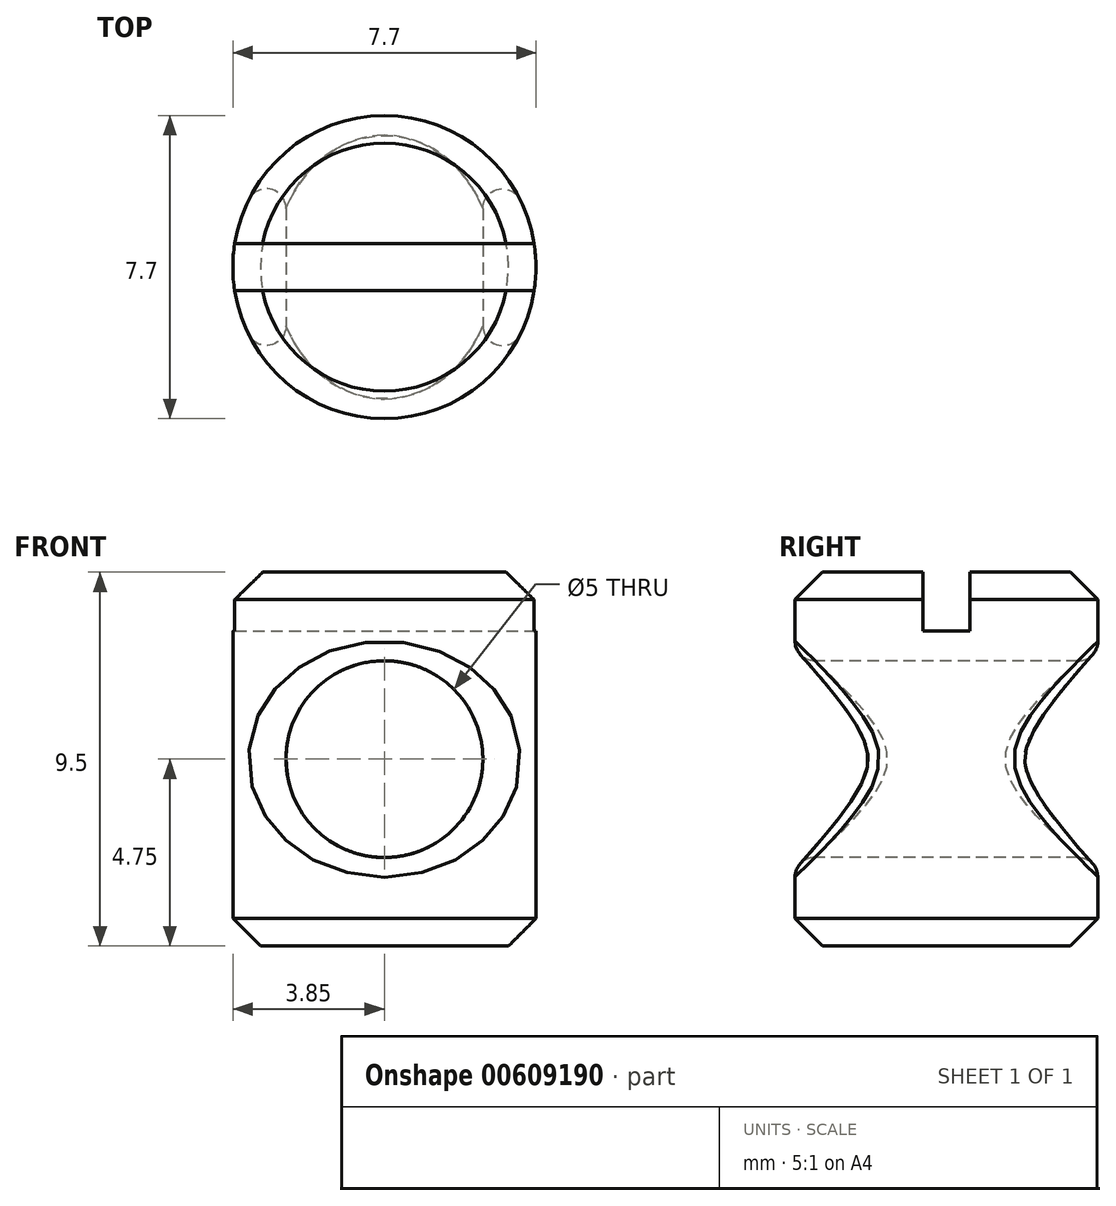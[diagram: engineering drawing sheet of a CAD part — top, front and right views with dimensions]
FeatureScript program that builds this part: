
annotation { "Feature Type Name" : "Feature", "Feature Type Description" : "" }
export const myFeature = defineFeature(function(context is Context, id is Id, definition is map)
    precondition{}
    {
        {
            var Q0;
            Q0=qCreatedBy(makeId("Top.planeOp"),FACE);
            var sketch = newSketch(context, id + "F0", { "sketchPlane" : qUnion([Q0])});
            skCircle(sketch, "E0", {"center": v(0, 0) * mm, "radius": 3.85 * mm});
            skSolve(sketch);
        }
        {
            var Q0;
            Q0=qSketchRegion(id+"F0",true);
            extrude(context, id + "F1", {"entities" : qUnion([Q0]), "depth" : 9.5 * mm, "offsetDistance" : 25 * mm});
        }
        {
            var Q0;
            Q0=qCreatedBy(makeId("Front.planeOp"),FACE);
            var sketch = newSketch(context, id + "F2", { "sketchPlane" : qUnion([Q0])});
            skCircle(sketch, "E1", {"center": v(0, 4.75) * mm, "radius": 2.5 * mm});
            skSolve(sketch);
        }
        {
            var Q0;
            Q0=qSketchRegion(id+"F2",true);
            extrude(context, id + "F3", {"entities" : qUnion([Q0]), "operationType" : NewBodyOperationType.REMOVE, "endBound" : BoundingType.SYMMETRIC, "oppositeDirection" : true, "depth" : 25 * mm, "offsetDistance" : 25 * mm});
        }
        {
            var Q0;
            Q0=makeQuery(id+"F1.opExtrude","CAP_FACE",FACE,{"disambiguationData":[OSD([sQuery(id+"F0.wireOp",EDGE,"E0")])],"isStart":false});
            var sketch = newSketch(context, id + "F4", { "sketchPlane" : qUnion([Q0])});
            skLineSegment(sketch, "E2.bottom", {"start": v(-4.71, 0.6) * mm, "end": v(4.71, 0.6) * mm});
            skLineSegment(sketch, "E2.top", {"start": v(-4.71, -0.6) * mm, "end": v(4.71, -0.6) * mm});
            skLineSegment(sketch, "E2.left", {"start": v(-4.71, 0.6) * mm, "end": v(-4.71, -0.6) * mm});
            skLineSegment(sketch, "E2.right", {"start": v(4.71, 0.6) * mm, "end": v(4.71, -0.6) * mm});
            skLineSegment(sketch, "E3", {"start": v(-4.71, 0) * mm, "end": v(0, 0) * mm, "construction": true});
            skLineSegment(sketch, "E4", {"start": v(0, 0) * mm, "end": v(0, 0.6) * mm, "construction": true});
            skPoint(sketch, "E4.endSnap0", {"position": v(0, 0.6) * mm});
            skSolve(sketch);
        }
        {
            var Q0;
            Q0=qSketchRegion(id+"F4",true);
            extrude(context, id + "F5", {"entities" : qUnion([Q0]), "operationType" : NewBodyOperationType.REMOVE, "oppositeDirection" : true, "depth" : 1.5 * mm, "offsetDistance" : 25 * mm});
        }
        {
            var Q0;
            {var subQ0=sQuery(id+"F0.wireOp",EDGE,"E0");Q0=makeQuery(id+"F5.boolean.opBoolean","SPLIT",EDGE,{"disambiguationData":[TD([makeQuery(id+"F5.opExtrude","SWEPT_FACE",FACE,{"disambiguationData":[OSD([sQuery(id+"F4.wireOp",EDGE,"E2.top")])]})])],"derivedFrom":makeQuery(id+"F1.opExtrude","CAP_EDGE",EDGE,{"disambiguationData":[OSD([subQ0])],"isStart":false})});}
            var Q1;
            {var subQ0=sQuery(id+"F0.wireOp",EDGE,"E0");Q1=makeQuery(id+"F5.boolean.opBoolean","SPLIT",EDGE,{"disambiguationData":[TD([makeQuery(id+"F5.opExtrude","SWEPT_FACE",FACE,{"disambiguationData":[OSD([sQuery(id+"F4.wireOp",EDGE,"E2.bottom")])]})])],"derivedFrom":makeQuery(id+"F1.opExtrude","CAP_EDGE",EDGE,{"disambiguationData":[OSD([subQ0])],"isStart":false})});}
            var Q2;
            Q2=makeQuery(id+"F1.opExtrude","CAP_EDGE",EDGE,{"disambiguationData":[OSD([sQuery(id+"F0.wireOp",EDGE,"E0")])],"isStart":true});
            chamfer(context, id + "F6", {"entities" : qUnion([Q0, Q1, Q2]), "width" : 0.7 * mm, "tangentPropagation" : true});
        }
        {
            var Q0;
            Q0=makeQuery(id+"F3.boolean.opBoolean","COPY",FACE,{"derivedFrom":makeQuery(id+"F3.opExtrude","SWEPT_FACE",FACE,{"disambiguationData":[OSD([sQuery(id+"F2.wireOp",EDGE,"E1")])]})});
            fillet(context, id + "F7", {"entities" : qUnion([Q0]), "radius" : .5 * mm, "tangentPropagation" : true, "allowEdgeOverflow" : false});
        }
    });
